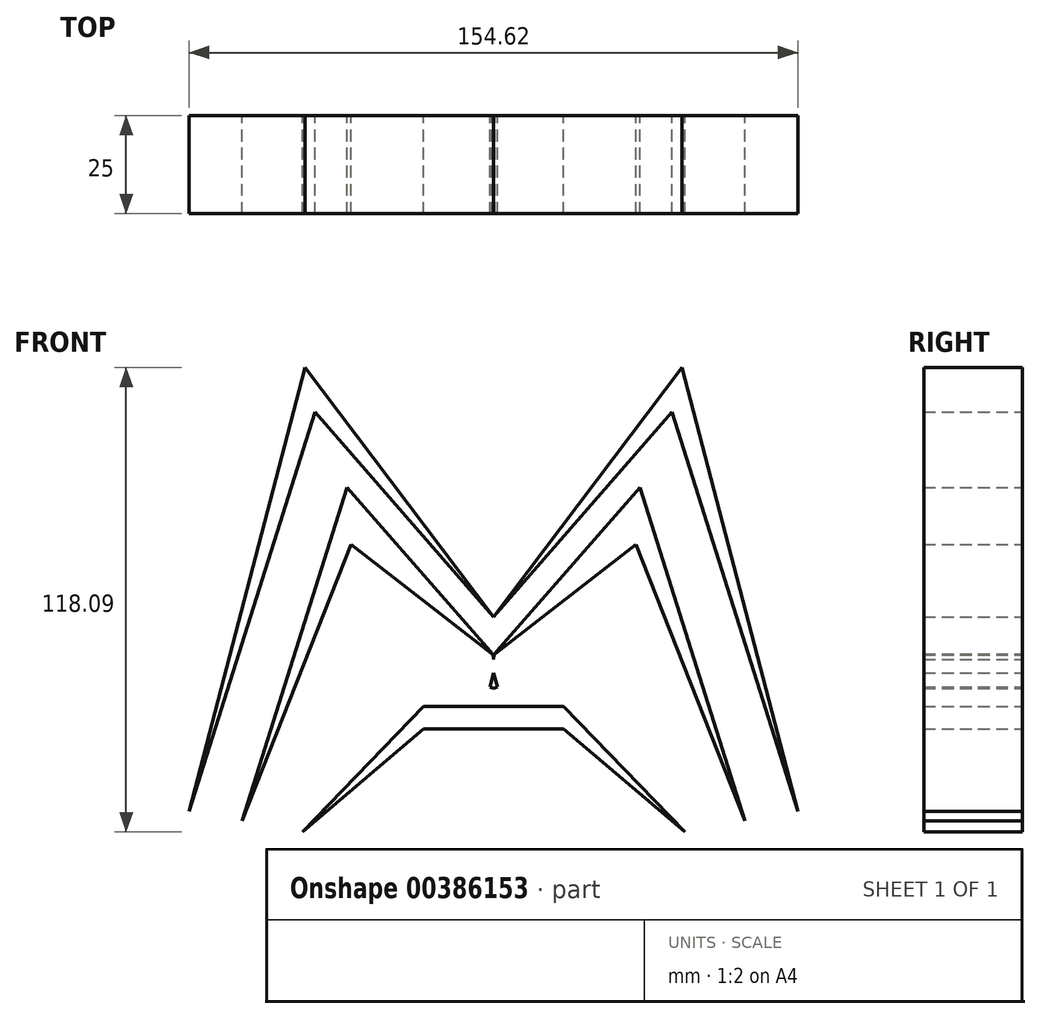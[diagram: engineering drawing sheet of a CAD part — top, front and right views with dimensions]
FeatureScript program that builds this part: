
annotation { "Feature Type Name" : "Feature", "Feature Type Description" : "" }
export const myFeature = defineFeature(function(context is Context, id is Id, definition is map)
    precondition{}
    {
        {
            var Q0;
            Q0=qCreatedBy(makeId("Front.planeOp"),FACE);
            var sketch = newSketch(context, id + "F0", { "sketchPlane" : qUnion([Q0])});
            skLineSegment(sketch, "E0", {"start": v(-0.74, 0.85) * mm, "end": v(-37.23, 42.55) * mm});
            skLineSegment(sketch, "E1", {"start": v(-37.23, 42.55) * mm, "end": v(-63.83, -42.2) * mm});
            skLineSegment(sketch, "E2", {"start": v(-63.83, -42.2) * mm, "end": v(-36.17, 28.01) * mm});
            skLineSegment(sketch, "E3", {"start": v(-36.17, 28.01) * mm, "end": v(0, 0) * mm});
            skLineSegment(sketch, "E4", {"start": v(0, -1.13) * mm, "end": v(0, 0) * mm});
            skPoint(sketch, "E5.visualSharp", {"position": v(0, 0) * mm});
            skArc(sketch, "E5.filletArc", {"start": v(0, -1.13) * mm, "mid": v(-0.2, -0.07) * mm, "end": v(-0.74, 0.85) * mm});
            skArc(sketch, "E6.MirrorCS", {"start": v(0, -1.13) * mm, "mid": v(0.2, -0.07) * mm, "end": v(0.74, 0.85) * mm});
            skLineSegment(sketch, "E7.MirrorCS", {"start": v(0.74, 0.85) * mm, "end": v(37.23, 42.55) * mm});
            skLineSegment(sketch, "E8.MirrorCS", {"start": v(37.23, 42.55) * mm, "end": v(63.83, -42.2) * mm});
            skLineSegment(sketch, "E9.MirrorCS", {"start": v(63.83, -42.2) * mm, "end": v(36.17, 28.01) * mm});
            skLineSegment(sketch, "E10.MirrorCS", {"start": v(36.17, 28.01) * mm, "end": v(0, 0) * mm});
            skLineSegment(sketch, "E11", {"start": v(0, -4.6) * mm, "end": v(-26.24, 7.45) * mm});
            skLineSegment(sketch, "E12", {"start": v(-26.24, 7.45) * mm, "end": v(-56.03, -43.26) * mm});
            skLineSegment(sketch, "E13", {"start": v(-56.03, -43.26) * mm, "end": v(-22.34, -1.13) * mm});
            skLineSegment(sketch, "E14", {"start": v(-22.34, 1.06) * mm, "end": v(0, -8.51) * mm});
            skLineSegment(sketch, "E15", {"start": v(-1.06, -8.51) * mm, "end": v(0, -4.6) * mm});
            skLineSegment(sketch, "E16.MirrorCS", {"start": v(1.06, -8.51) * mm, "end": v(0, -4.6) * mm});
            skLineSegment(sketch, "E17.MirrorCS", {"start": v(0, -4.6) * mm, "end": v(26.24, 7.45) * mm});
            skLineSegment(sketch, "E18.MirrorCS", {"start": v(26.24, 7.45) * mm, "end": v(56.03, -43.26) * mm});
            skLineSegment(sketch, "E19.MirrorCS", {"start": v(56.03, -43.26) * mm, "end": v(22.34, -1.13) * mm});
            skLineSegment(sketch, "E20.MirrorCS", {"start": v(22.34, 1.06) * mm, "end": v(0, -8.51) * mm});
            skLineSegment(sketch, "E21", {"start": v(1.06, -13.12) * mm, "end": v(-17.73, -13.12) * mm});
            skLineSegment(sketch, "E22", {"start": v(-17.73, -13.12) * mm, "end": v(-48.58, -45.04) * mm});
            skLineSegment(sketch, "E23", {"start": v(-48.58, -45.04) * mm, "end": v(-17.73, -18.8) * mm});
            skLineSegment(sketch, "E24", {"start": v(-17.73, -18.8) * mm, "end": v(1.06, -18.8) * mm});
            skLineSegment(sketch, "E25", {"start": v(1.06, -18.8) * mm, "end": v(1.06, -13.12) * mm});
            skLineSegment(sketch, "E26.MirrorCS", {"start": v(-1.06, -18.8) * mm, "end": v(-1.06, -13.12) * mm});
            skLineSegment(sketch, "E27.MirrorCS", {"start": v(48.58, -45.04) * mm, "end": v(17.73, -18.8) * mm});
            skLineSegment(sketch, "E28.MirrorCS", {"start": v(-1.06, -13.12) * mm, "end": v(17.73, -13.12) * mm});
            skLineSegment(sketch, "E29.MirrorCS", {"start": v(17.73, -18.8) * mm, "end": v(-1.06, -18.8) * mm});
            skLineSegment(sketch, "E30.MirrorCS", {"start": v(17.73, -13.12) * mm, "end": v(48.58, -45.04) * mm});
            skLineSegment(sketch, "E31", {"start": v(0, 9.57) * mm, "end": v(-47.87, 73.05) * mm});
            skLineSegment(sketch, "E32", {"start": v(-47.87, 73.05) * mm, "end": v(-77.3, -39.72) * mm});
            skLineSegment(sketch, "E33", {"start": v(-77.3, -39.72) * mm, "end": v(-45.4, 61.7) * mm});
            skLineSegment(sketch, "E34", {"start": v(-45.4, 61.7) * mm, "end": v(0, 9.57) * mm});
            skLineSegment(sketch, "E35.MirrorCS", {"start": v(45.4, 61.7) * mm, "end": v(0, 9.57) * mm});
            skLineSegment(sketch, "E36.MirrorCS", {"start": v(47.87, 73.05) * mm, "end": v(77.3, -39.72) * mm});
            skLineSegment(sketch, "E37.MirrorCS", {"start": v(77.3, -39.72) * mm, "end": v(45.4, 61.7) * mm});
            skLineSegment(sketch, "E38.MirrorCS", {"start": v(0, 9.57) * mm, "end": v(47.87, 73.05) * mm});
            skSolve(sketch);
        }
        {
            var Q0;
            Q0 = qSketchRegion(id + "F0", true);
            extrude(context, id + "F1", {"entities" : qUnion([Q0]), "depth" : 25 * mm});
        }
    });
